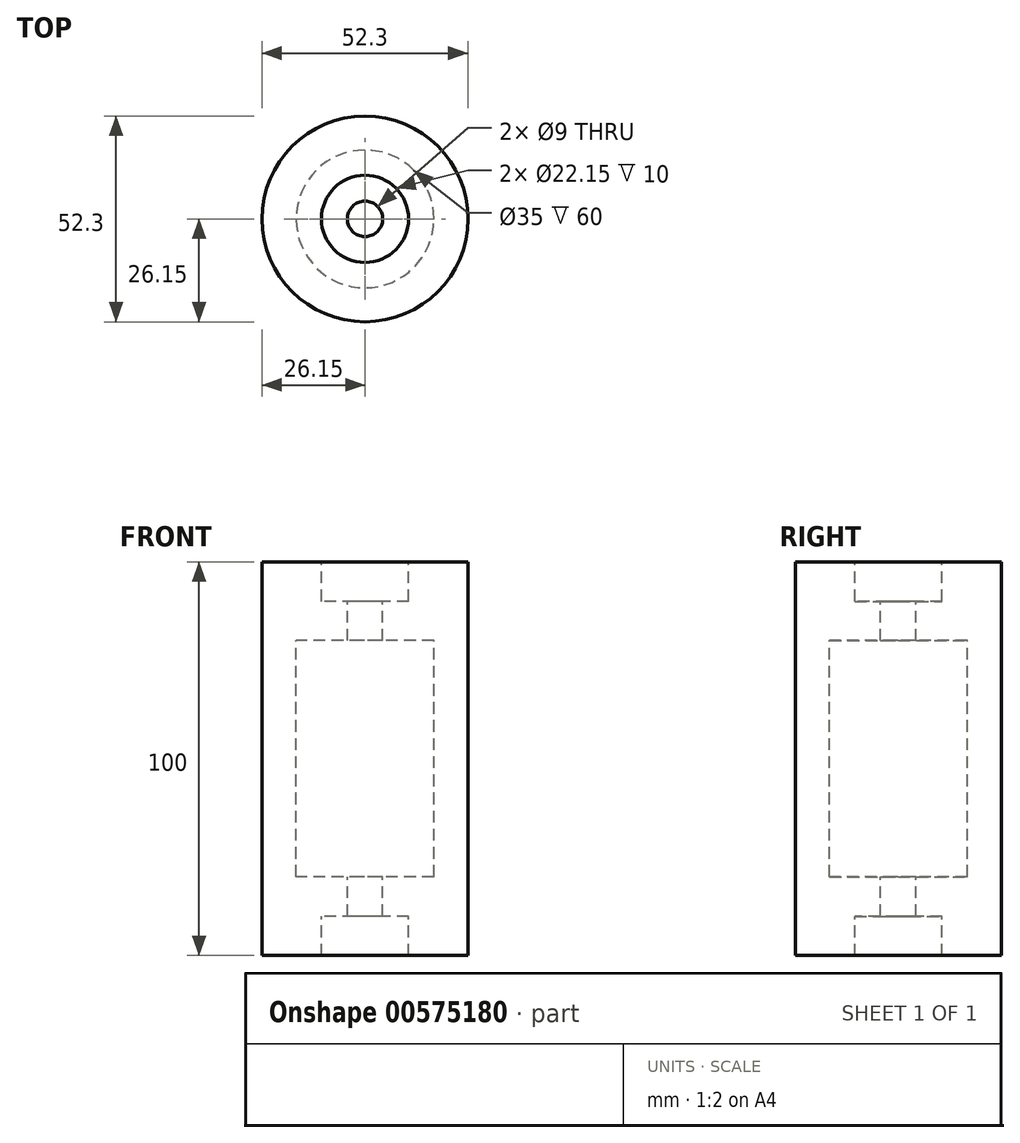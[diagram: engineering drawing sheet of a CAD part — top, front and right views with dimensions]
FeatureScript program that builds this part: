
annotation { "Feature Type Name" : "Feature", "Feature Type Description" : "" }
export const myFeature = defineFeature(function(context is Context, id is Id, definition is map)
    precondition{}
    {
        {
            var Q0;
            Q0=qCreatedBy(makeId("Top.planeOp"),FACE);
            var sketch = newSketch(context, id + "F0", { "sketchPlane" : qUnion([Q0])});
            skCircle(sketch, "E0", {"center": v(0, 0) * mm, "radius": 26.15 * mm});
            skSolve(sketch);
        }
        {
            var Q0;
            Q0=makeQuery(id+"F0.imprint","IMPRINT",FACE,{"disambiguationData":[TD([[makeQuery(id+"F0.imprint","IMPRINT",EDGE,{"derivedFrom":sQuery(id+"F0.wireOp",EDGE,"E0")}),1.0]])]});
            extrude(context, id + "F1", {"entities" : qUnion([Q0]), "depth" : 100 * mm, "offsetDistance" : 25 * mm});
        }
        {
            var Q0;
            Q0=makeQuery(id+"F1.opExtrude","CAP_FACE",FACE,{"disambiguationData":[OSD([sQuery(id+"F0.wireOp",EDGE,"E0")])],"isStart":false});
            var sketch = newSketch(context, id + "F2", { "sketchPlane" : qUnion([Q0])});
            skCircle(sketch, "E1", {"center": v(0, 0) * mm, "radius": 11.07 * mm});
            skSolve(sketch);
        }
        {
            var Q0;
            Q0 = qSketchRegion(id + "F2", true);
            var Q1;
            Q1=makeQuery(id+"F1.opExtrude","CAP_FACE",FACE,{"disambiguationData":[OSD([sQuery(id+"F0.wireOp",EDGE,"E0")])],"isStart":true});
            extrude(context, id + "F3", {"entities" : qUnion([Q0]), "operationType" : NewBodyOperationType.REMOVE, "endBound" : BoundingType.UP_TO_SURFACE, "oppositeDirection" : true, "depth" : 25 * mm, "endBoundEntityFace" : qUnion([Q1]), "offsetDistance" : 25 * mm});
        }
        {
            var Q0;
            Q0=makeQuery(id+"F1.opExtrude","CAP_FACE",FACE,{"disambiguationData":[OSD([sQuery(id+"F0.wireOp",EDGE,"E0")])],"isStart":false});
            cPlane(context, id + "F4", {"entities" : qUnion([Q0]), "cplaneType" : CPlaneType.OFFSET, "offset" : 10 * mm, "oppositeDirection" : true, "width" : 150 * mm, "height" : 150 * mm});
        }
        {
            var Q0;
            Q0=qCreatedBy(id+"F4.planeOp",FACE);
            var sketch = newSketch(context, id + "F5", { "sketchPlane" : qUnion([Q0])});
            skCircle(sketch, "E2", {"center": v(0, 0) * mm, "radius": 4.5 * mm});
            skCircle(sketch, "E3", {"center": v(0, 0) * mm, "radius": 11.08 * mm});
            skSolve(sketch);
        }
        {
            var Q0;
            Q0=makeQuery(id+"F5.imprint","IMPRINT",FACE,{"disambiguationData":[TD([[makeQuery(id+"F5.imprint","IMPRINT",EDGE,{"derivedFrom":sQuery(id+"F5.wireOp",EDGE,"E2")}),-1.0]])]});
            extrude(context, id + "F6", {"entities" : qUnion([Q0]), "operationType" : NewBodyOperationType.ADD, "oppositeDirection" : true, "depth" : 80 * mm, "offsetDistance" : 25 * mm});
        }
        {
            var Q0;
            Q0=qCreatedBy(id+"F4.planeOp",FACE);
            cPlane(context, id + "F7", {"entities" : qUnion([Q0]), "cplaneType" : CPlaneType.OFFSET, "offset" : 10 * mm, "oppositeDirection" : true, "width" : 150 * mm, "height" : 150 * mm});
        }
        {
            var Q0;
            Q0=qCreatedBy(id+"F7.planeOp",FACE);
            var sketch = newSketch(context, id + "F8", { "sketchPlane" : qUnion([Q0])});
            skCircle(sketch, "E4", {"center": v(0, 0) * mm, "radius": 17.5 * mm});
            skSolve(sketch);
        }
        {
            var Q0;
            Q0 = qSketchRegion(id + "F8", true);
            extrude(context, id + "F9", {"entities" : qUnion([Q0]), "operationType" : NewBodyOperationType.REMOVE, "oppositeDirection" : true, "depth" : 60 * mm, "offsetDistance" : 25 * mm});
        }
    });
